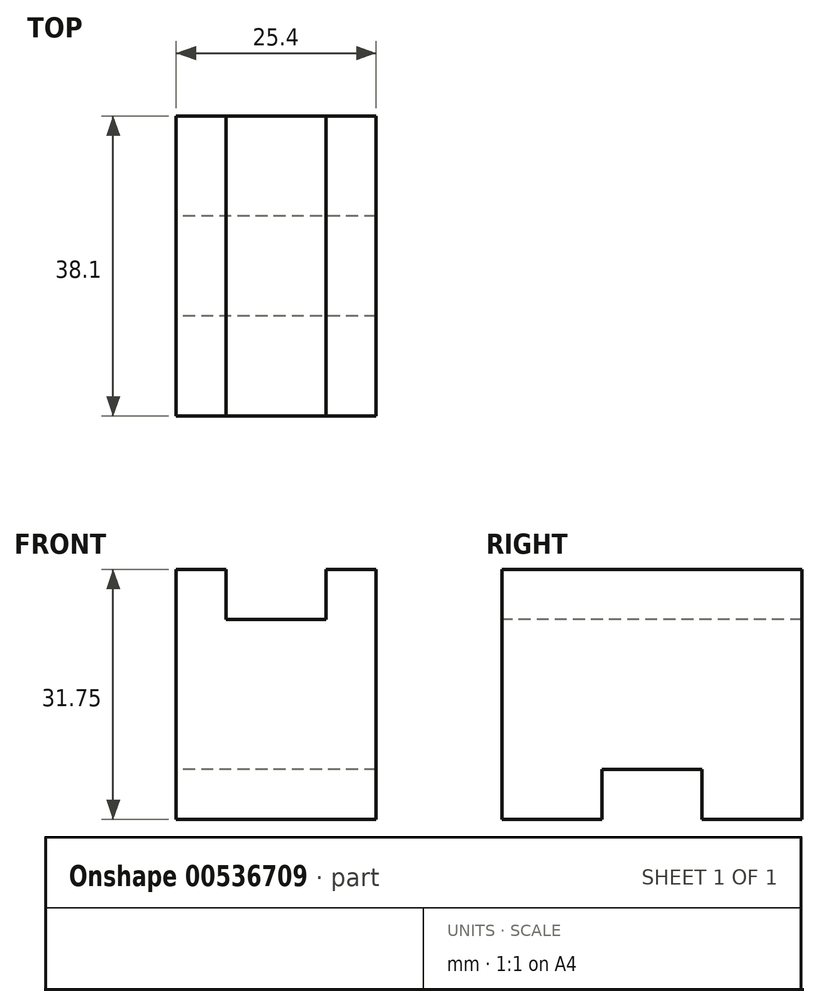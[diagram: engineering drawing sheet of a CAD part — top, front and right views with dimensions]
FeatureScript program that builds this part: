
annotation { "Feature Type Name" : "Feature", "Feature Type Description" : "" }
export const myFeature = defineFeature(function(context is Context, id is Id, definition is map)
    precondition{}
    {
        {
            var Q0;
            Q0=qCreatedBy(makeId("Front.planeOp"),FACE);
            var sketch = newSketch(context, id + "F0", { "sketchPlane" : qUnion([Q0])});
            skLineSegment(sketch, "E0", {"start": v(-54.2, 54.62) * mm, "end": v(-54.2, 22.87) * mm});
            skLineSegment(sketch, "E1", {"start": v(-54.2, 22.87) * mm, "end": v(-28.8, 22.87) * mm});
            skLineSegment(sketch, "E2", {"start": v(-28.8, 22.87) * mm, "end": v(-28.8, 54.62) * mm});
            skLineSegment(sketch, "E3", {"start": v(-28.8, 54.62) * mm, "end": v(-54.2, 54.62) * mm});
            skSolve(sketch);
        }
        {
            var Q0;
            Q0=makeQuery(id+"F0.imprint","IMPRINT",FACE,{"disambiguationData":[TD([[makeQuery(id+"F0.imprint","IMPRINT",EDGE,{"derivedFrom":sQuery(id+"F0.wireOp",EDGE,"E0")}),1.0]])]});
            extrude(context, id + "F1", {"entities" : qUnion([Q0]), "depth" : 38.1 * mm, "offsetDistance" : 25.4 * mm});
        }
        {
            var Q0;
            Q0=makeQuery(id+"F1.opExtrude","CAP_FACE",FACE,{"disambiguationData":[OSD([sQuery(id+"F0.wireOp",EDGE,"E0"),sQuery(id+"F0.wireOp",EDGE,"E1"),sQuery(id+"F0.wireOp",EDGE,"E2"),sQuery(id+"F0.wireOp",EDGE,"E3")])],"isStart":false});
            var sketch = newSketch(context, id + "F2", { "sketchPlane" : qUnion([Q0])});
            skLineSegment(sketch, "E4", {"start": v(-47.85, 54.62) * mm, "end": v(-47.85, 48.27) * mm});
            skLineSegment(sketch, "E5", {"start": v(-47.85, 48.27) * mm, "end": v(-35.15, 48.27) * mm});
            skLineSegment(sketch, "E6", {"start": v(-35.15, 48.27) * mm, "end": v(-35.15, 54.62) * mm});
            skLineSegment(sketch, "E7", {"start": v(-35.15, 54.62) * mm, "end": v(-47.85, 54.62) * mm});
            skSolve(sketch);
        }
        {
            var Q0;
            Q0=makeQuery(id+"F2.imprint","IMPRINT",FACE,{"disambiguationData":[TD([[makeQuery(id+"F2.imprint","IMPRINT",EDGE,{"derivedFrom":sQuery(id+"F2.wireOp",EDGE,"E4")}),1.0]])]});
            extrude(context, id + "F3", {"entities" : qUnion([Q0]), "operationType" : NewBodyOperationType.REMOVE, "oppositeDirection" : true, "depth" : 38.1 * mm, "offsetDistance" : 25.4 * mm});
        }
        {
            var Q0;
            Q0=makeQuery(id+"F1.opExtrude","SWEPT_FACE",FACE,{"disambiguationData":[OSD([sQuery(id+"F0.wireOp",EDGE,"E0")])]});
            var sketch = newSketch(context, id + "F4", { "sketchPlane" : qUnion([Q0])});
            skLineSegment(sketch, "E8", {"start": v(12.7, 22.87) * mm, "end": v(12.7, 29.22) * mm});
            skLineSegment(sketch, "E9", {"start": v(12.7, 29.22) * mm, "end": v(25.4, 29.22) * mm});
            skLineSegment(sketch, "E10", {"start": v(25.4, 29.22) * mm, "end": v(25.4, 22.87) * mm});
            skSolve(sketch);
        }
        {
            var Q0;
            {var subQ0=sQuery(id+"F4.wireOp",EDGE,"E8");Q0=makeQuery(id+"F4.imprint","IMPRINT",FACE,{"disambiguationData":[TD([[makeQuery(id+"F4.imprint","IMPRINT",EDGE,{"derivedFrom":subQ0}),-1.0]])]});}
            extrude(context, id + "F5", {"entities" : qUnion([Q0]), "operationType" : NewBodyOperationType.REMOVE, "oppositeDirection" : true, "depth" : 25.4 * mm, "offsetDistance" : 25.4 * mm});
        }
    });
